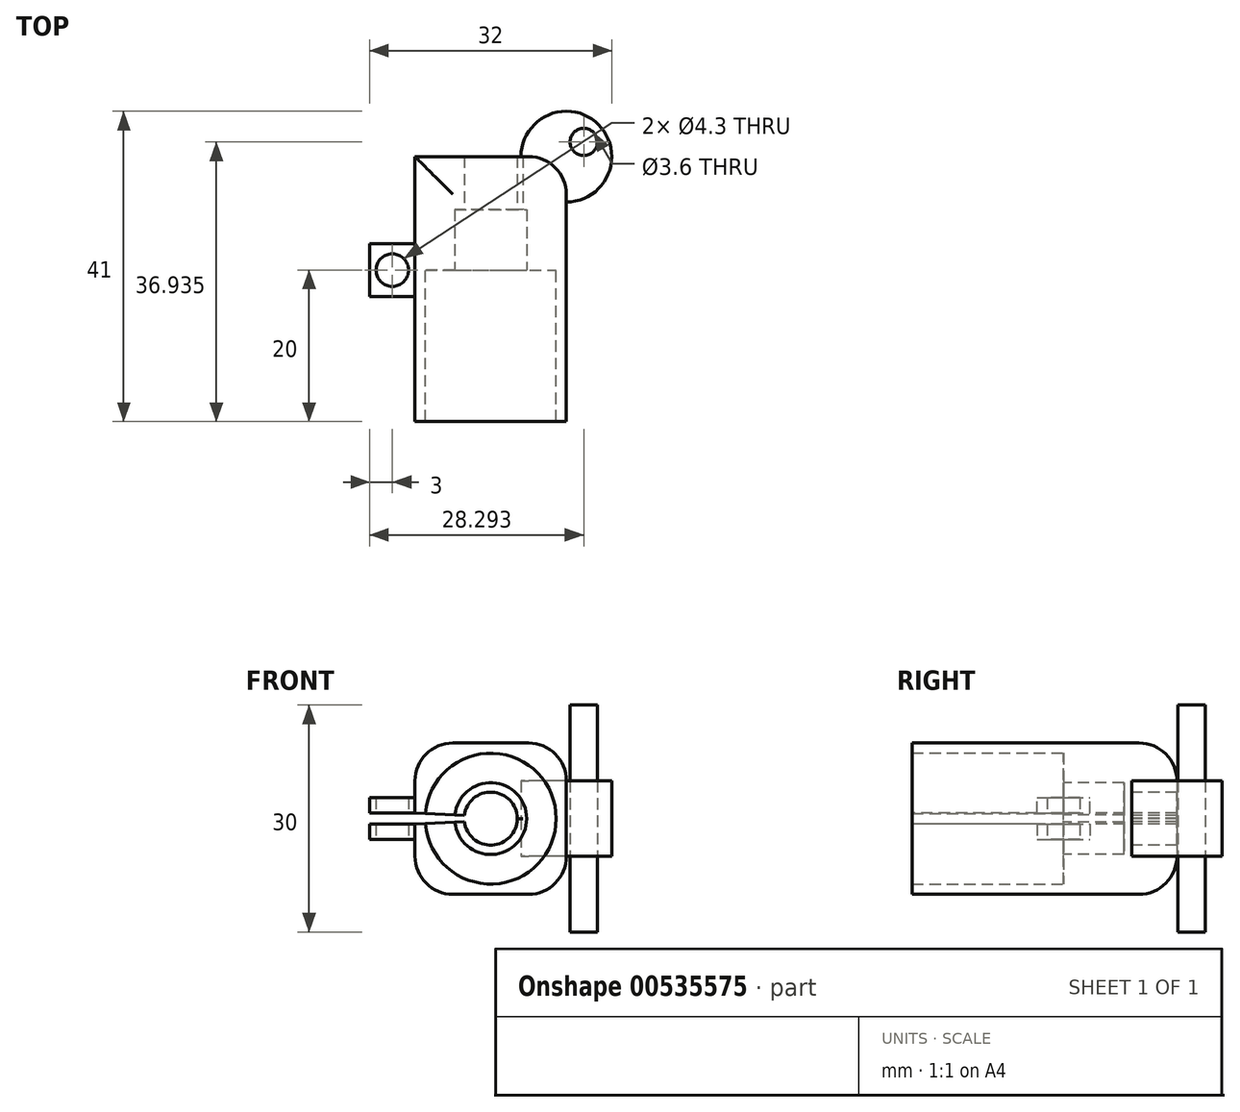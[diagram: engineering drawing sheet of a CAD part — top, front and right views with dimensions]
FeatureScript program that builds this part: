
annotation { "Feature Type Name" : "Feature", "Feature Type Description" : "" }
export const myFeature = defineFeature(function(context is Context, id is Id, definition is map)
    precondition{}
    {
        {
            var Q0;
            Q0=qCreatedBy(makeId("Front.planeOp"),FACE);
            var sketch = newSketch(context, id + "F0", { "sketchPlane" : qUnion([Q0])});
            skCircle(sketch, "E0", {"center": v(0, 0) * mm, "radius": 8.65 * mm});
            skLineSegment(sketch, "E1.bottom", {"start": v(-10, 10) * mm, "end": v(10, 10) * mm});
            skLineSegment(sketch, "E1.top", {"start": v(-10, -10) * mm, "end": v(10, -10) * mm});
            skLineSegment(sketch, "E1.left", {"start": v(-10, 10) * mm, "end": v(-10, -10) * mm});
            skLineSegment(sketch, "E1.right", {"start": v(10, 10) * mm, "end": v(10, -10) * mm});
            skSolve(sketch);
        }
        {
            var Q0;
            Q0 = qSketchRegion(id + "F0", true);
            extrude(context, id + "F1", {"entities" : qUnion([Q0]), "depth" : 20 * mm, "offsetDistance" : 25 * mm});
        }
        {
            var Q0;
            Q0=qCreatedBy(makeId("Front.planeOp"),FACE);
            var sketch = newSketch(context, id + "F2", { "sketchPlane" : qUnion([Q0])});
            skLineSegment(sketch, "E2.bottom", {"start": v(10, 10) * mm, "end": v(-10, 10) * mm});
            skLineSegment(sketch, "E2.top", {"start": v(10, -10) * mm, "end": v(-10, -10) * mm});
            skLineSegment(sketch, "E2.left", {"start": v(10, 10) * mm, "end": v(10, -10) * mm});
            skLineSegment(sketch, "E2.right", {"start": v(-10, 10) * mm, "end": v(-10, -10) * mm});
            skPoint(sketch, "E2.middle", {"position": v(0, 0) * mm});
            skSolve(sketch);
        }
        {
            var Q0;
            Q0 = qSketchRegion(id + "F2", true);
            extrude(context, id + "F3", {"entities" : qUnion([Q0]), "operationType" : NewBodyOperationType.ADD, "oppositeDirection" : true, "depth" : 15 * mm, "offsetDistance" : 25 * mm});
        }
        {
            var Q0;
            Q0=qCreatedBy(makeId("Front.planeOp"),FACE);
            var sketch = newSketch(context, id + "F4", { "sketchPlane" : qUnion([Q0])});
            skCircle(sketch, "E3", {"center": v(0, 0) * mm, "radius": 4.75 * mm});
            skSolve(sketch);
        }
        {
            var Q0;
            Q0 = qSketchRegion(id + "F4", true);
            extrude(context, id + "F5", {"entities" : qUnion([Q0]), "operationType" : NewBodyOperationType.REMOVE, "oppositeDirection" : true, "depth" : 8 * mm, "offsetDistance" : 25 * mm});
        }
        {
            var Q0;
            Q0=qCreatedBy(makeId("Front.planeOp"),FACE);
            var sketch = newSketch(context, id + "F6", { "sketchPlane" : qUnion([Q0])});
            skCircle(sketch, "E4", {"center": v(0, 0) * mm, "radius": 2.08 * mm});
            skSolve(sketch);
        }
        {
            var Q0;
            Q0 = qSketchRegion(id + "F6", true);
            extrude(context, id + "F7", {"entities" : qUnion([Q0]), "operationType" : NewBodyOperationType.REMOVE, "oppositeDirection" : true, "depth" : 11 * mm, "offsetDistance" : 25 * mm});
        }
        {
            var Q0;
            Q0=qCreatedBy(makeId("Front.planeOp"),FACE);
            var sketch = newSketch(context, id + "F8", { "sketchPlane" : qUnion([Q0])});
            skLineSegment(sketch, "E5.left", {"start": v(-10, 0.75) * mm, "end": v(-10, -0.75) * mm});
            skLineSegment(sketch, "E6", {"start": v(4.25, 0) * mm, "end": v(-10, 0.75) * mm});
            skLineSegment(sketch, "E7", {"start": v(4.25, 0) * mm, "end": v(-10, -0.75) * mm});
            skSolve(sketch);
        }
        {
            var Q0;
            Q0 = qSketchRegion(id + "F8", true);
            extrude(context, id + "F9", {"entities" : qUnion([Q0]), "operationType" : NewBodyOperationType.REMOVE, "oppositeDirection" : true, "depth" : 50.6 * mm, "offsetDistance" : 25 * mm, "symmetric" : true});
        }
        {
            var Q0;
            Q0=qCreatedBy(makeId("Front.planeOp"),FACE);
            var sketch = newSketch(context, id + "F10", { "sketchPlane" : qUnion([Q0])});
            skLineSegment(sketch, "E8.bottom", {"start": v(-10, 0.75) * mm, "end": v(-16, 0.75) * mm});
            skLineSegment(sketch, "E8.top", {"start": v(-10, 2.75) * mm, "end": v(-16, 2.75) * mm});
            skLineSegment(sketch, "E8.left", {"start": v(-10, 0.75) * mm, "end": v(-10, 2.75) * mm});
            skLineSegment(sketch, "E8.right", {"start": v(-16, 0.75) * mm, "end": v(-16, 2.75) * mm});
            skLineSegment(sketch, "E9.bottom", {"start": v(-10, -0.75) * mm, "end": v(-16, -0.75) * mm});
            skLineSegment(sketch, "E9.top", {"start": v(-10, -2.75) * mm, "end": v(-16, -2.75) * mm});
            skLineSegment(sketch, "E9.left", {"start": v(-10, -0.75) * mm, "end": v(-10, -2.75) * mm});
            skLineSegment(sketch, "E9.right", {"start": v(-16, -0.75) * mm, "end": v(-16, -2.75) * mm});
            skSolve(sketch);
        }
        {
            var Q0;
            Q0 = qSketchRegion(id + "F10", true);
            extrude(context, id + "F11", {"entities" : qUnion([Q0]), "operationType" : NewBodyOperationType.ADD, "depth" : 7 * mm, "offsetDistance" : 25 * mm, "symmetric" : true});
        }
        {
            var Q0;
            Q0=qCreatedBy(makeId("Top.planeOp"),FACE);
            var sketch = newSketch(context, id + "F12", { "sketchPlane" : qUnion([Q0])});
            skCircle(sketch, "E10", {"center": v(-13, 0) * mm, "radius": 2.15 * mm});
            skSolve(sketch);
        }
        {
            var Q0;
            Q0 = qSketchRegion(id + "F12", true);
            extrude(context, id + "F13", {"entities" : qUnion([Q0]), "operationType" : NewBodyOperationType.REMOVE, "depth" : 10.46 * mm, "offsetDistance" : 25 * mm, "symmetric" : true});
        }
        {
            var Q0;
            Q0=qCreatedBy(makeId("Top.planeOp"),FACE);
            var sketch = newSketch(context, id + "F14", { "sketchPlane" : qUnion([Q0])});
            skCircle(sketch, "E11", {"center": v(-13, 0) * mm, "radius": 1.65 * mm});
            skSolve(sketch);
        }
        {
            var Q0;
            Q0 = qSketchRegion(id + "F14", true);
            extrude(context, id + "F15", {"entities" : qUnion([Q0]), "operationType" : NewBodyOperationType.REMOVE, "oppositeDirection" : true, "depth" : 6.34 * mm, "offsetDistance" : 25 * mm});
        }
        {
            var Q0;
            Q0=qCreatedBy(makeId("Top.planeOp"),FACE);
            var sketch = newSketch(context, id + "F16", { "sketchPlane" : qUnion([Q0])});
            skArc(sketch, "E12", {"start": v(10, 9) * mm, "mid": v(14.24, 19.24) * mm, "end": v(4, 15) * mm});
            skLineSegment(sketch, "E13", {"start": v(10, 9) * mm, "end": v(10, 15) * mm});
            skLineSegment(sketch, "E14", {"start": v(4, 15) * mm, "end": v(10, 15) * mm});
            skCircle(sketch, "E15", {"center": v(12.3, 16.93) * mm, "radius": 1.8 * mm});
            skSolve(sketch);
        }
        {
            var Q0;
            Q0=makeQuery(id+"F16.imprint","IMPRINT",FACE,{"disambiguationData":[TD([[makeQuery(id+"F16.imprint","IMPRINT",EDGE,{"derivedFrom":sQuery(id+"F16.wireOp",EDGE,"E12")}),1.0]])]});
            var Q1;
            Q1=sQuery(id+"F16.wireOp",EDGE,"E12");
            extrude(context, id + "F17", {"entities" : qUnion([Q0]), "operationType" : NewBodyOperationType.ADD, "surfaceEntities" : qUnion([Q1]), "depth" : 10 * mm, "offsetDistance" : 25 * mm, "symmetric" : true});
        }
        {
            var Q0;
            {var subQ0=sQuery(id+"F2.wireOp",EDGE,"E2.bottom");var subQ1=sQuery(id+"F2.wireOp",EDGE,"E2.left");Q0=makeQuery(id+"F17.boolean.opBoolean","SPLIT",EDGE,{"disambiguationData":[TD([makeQuery(id+"F3.opExtrude","SWEPT_FACE",FACE,{"disambiguationData":[OSD([subQ0])]})])],"derivedFrom":makeQuery(id+"F3.opExtrude","CAP_EDGE",EDGE,{"disambiguationData":[OSD([subQ1])],"isStart":false})});}
            fillet(context, id + "F18", {"entities" : qUnion([Q0]), "radius" : 5 * mm, "tangentPropagation" : true, "allowEdgeOverflow" : false});
        }
        {
            var Q0;
            {var subQ0=sQuery(id+"F2.wireOp",EDGE,"E2.left");var subQ1=sQuery(id+"F2.wireOp",EDGE,"E2.top");Q0=makeQuery(id+"F17.boolean.opBoolean","SPLIT",EDGE,{"disambiguationData":[TD([makeQuery(id+"F3.opExtrude","SWEPT_FACE",FACE,{"disambiguationData":[OSD([subQ1])]})])],"derivedFrom":makeQuery(id+"F3.opExtrude","CAP_EDGE",EDGE,{"disambiguationData":[OSD([subQ0])],"isStart":false})});}
            fillet(context, id + "F19", {"entities" : qUnion([Q0]), "radius" : 5 * mm, "tangentPropagation" : true, "allowEdgeOverflow" : false});
        }
        {
            var Q0;
            Q0=makeQuery(id+"F1.opExtrude","SWEPT_EDGE",EDGE,{"disambiguationData":[OSD([sQuery(id+"F0.wireOp",EDGE,"E1.top"),sQuery(id+"F0.wireOp",EDGE,"E1.left")])]});
            var Q1;
            Q1=makeQuery(id+"F1.opExtrude","SWEPT_EDGE",EDGE,{"disambiguationData":[OSD([sQuery(id+"F0.wireOp",EDGE,"E1.bottom"),sQuery(id+"F0.wireOp",EDGE,"E1.left")])]});
            var Q2;
            Q2=makeQuery(id+"F1.opExtrude","SWEPT_EDGE",EDGE,{"disambiguationData":[OSD([sQuery(id+"F0.wireOp",EDGE,"E1.top"),sQuery(id+"F0.wireOp",EDGE,"E1.right")])]});
            var Q3;
            Q3=makeQuery(id+"F1.opExtrude","SWEPT_EDGE",EDGE,{"disambiguationData":[OSD([sQuery(id+"F0.wireOp",EDGE,"E1.bottom"),sQuery(id+"F0.wireOp",EDGE,"E1.right")])]});
            var Q4;
            Q4=makeQuery(id+"F3.opExtrude","SWEPT_EDGE",EDGE,{"disambiguationData":[OSD([sQuery(id+"F2.wireOp",EDGE,"E2.bottom"),sQuery(id+"F2.wireOp",EDGE,"E2.left")])]});
            var Q5;
            Q5=makeQuery(id+"F3.opExtrude","SWEPT_EDGE",EDGE,{"disambiguationData":[OSD([sQuery(id+"F2.wireOp",EDGE,"E2.bottom"),sQuery(id+"F2.wireOp",EDGE,"E2.right")])]});
            var Q6;
            Q6=makeQuery(id+"F3.opExtrude","SWEPT_EDGE",EDGE,{"disambiguationData":[OSD([sQuery(id+"F2.wireOp",EDGE,"E2.top"),sQuery(id+"F2.wireOp",EDGE,"E2.right")])]});
            var Q7;
            Q7=makeQuery(id+"F3.opExtrude","SWEPT_EDGE",EDGE,{"disambiguationData":[OSD([sQuery(id+"F2.wireOp",EDGE,"E2.top"),sQuery(id+"F2.wireOp",EDGE,"E2.left")])]});
            fillet(context, id + "F20", {"entities" : qUnion([Q0, Q1, Q2, Q3, Q4, Q5, Q6, Q7]), "radius" : 5 * mm, "tangentPropagation" : true, "allowEdgeOverflow" : false});
        }
        {
            var Q0;
            Q0=qCreatedBy(makeId("Front.planeOp"),FACE);
            var sketch = newSketch(context, id + "F21", { "sketchPlane" : qUnion([Q0])});
            skCircle(sketch, "E16", {"center": v(0, 0) * mm, "radius": 3.5 * mm});
            skSolve(sketch);
        }
        {
            var Q0;
            Q0 = qSketchRegion(id + "F21", true);
            extrude(context, id + "F22", {"entities" : qUnion([Q0]), "operationType" : NewBodyOperationType.REMOVE, "oppositeDirection" : true, "depth" : 31.8 * mm, "offsetDistance" : 25 * mm});
        }
        {
            var Q0;
            Q0=qCreatedBy(makeId("Top.planeOp"),FACE);
            var sketch = newSketch(context, id + "F23", { "sketchPlane" : qUnion([Q0])});
            skCircle(sketch, "E17", {"center": v(12.3, 16.93) * mm, "radius": 1.8 * mm});
            skSolve(sketch);
        }
        {
            var Q0;
            Q0 = qSketchRegion(id + "F23", true);
            extrude(context, id + "F24", {"entities" : qUnion([Q0]), "depth" : 30 * mm, "offsetDistance" : 25 * mm, "symmetric" : true});
        }
    });
